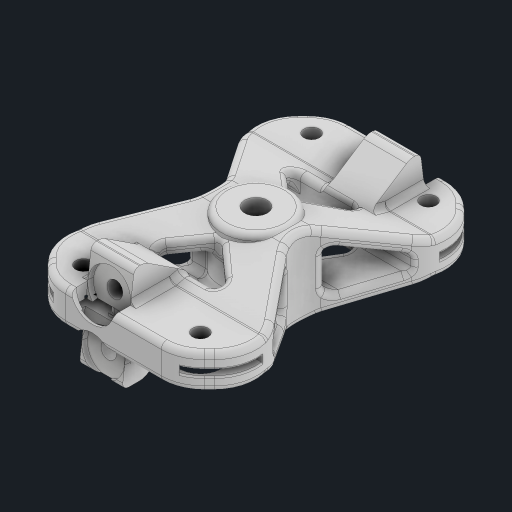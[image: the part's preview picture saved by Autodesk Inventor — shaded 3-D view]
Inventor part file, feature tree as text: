
AUTODESK INVENTOR PART (.ipt)
format: ipt  version: 2023 (Build 270158000, 158)  size: 2,082,816 bytes
history: native  units: mm
features: extrude x25, fillet x22, sketch x9, chamfer x6, mirror x2, plane x1, loft x1, other x1
ambient origin geometry x8: Origin, YZ Plane, XZ Plane, XY Plane, X Axis, Y Axis, Z Axis, Center Point
bodies: Body1 (feature_tree)
feature tree (67):
  sketch  "Sketch1"  dims[d13=261.822mm d14=7.45mm]
  plane  "Work Plane1"
  sketch  "Sketch2"  dims[d15=27.223mm d17=1.0mm]
  extrude  "Extrusion26"  Depth=7.45mm
  extrude  "Extrusion27"  Depth=1.0mm
  loft  "Loft4"
  extrude  "Extrusion30"  Depth=1.0mm
  chamfer  "Chamfer7"  Distance=15.0mm
  chamfer  "Chamfer8"  Distance=1.0mm
  extrude  "Extrusion45"  Depth=0.5mm
  extrude  "Extrusion55"  Depth=0.5mm TaperAngle=0.0deg
  extrude  "Extrusion57"  Depth=0.5mm
  sketch  "Sketch19"  dims[d26=90.0deg]
  extrude  "Extrusion67"  Depth=0.5mm
  extrude  "Extrusion68"  Depth=0.5mm TaperAngle=0.0deg
  mirror  "Mirror6"
  extrude  "Extrusion69"  Depth=0.5mm TaperAngle=0.0deg
  chamfer  "Chamfer18"  Distance=19.96mm
  chamfer  "Chamfer19"  Angle=90.0deg  [1 undecoded]
  chamfer  "Chamfer20"  Angle=90.0deg  [1 undecoded]
  chamfer  "Chamfer21"  Distance=2.0mm
  sketch  "Sketch23"  dims[d28=90.0deg d29=5.5mm d30=15.0mm]
  extrude  "Extrusion71"  Depth=2.0mm
  extrude  "Extrusion72"  Depth=0.5mm TaperAngle=45.0deg
  fillet  "Fillet54"  Radius=12.0mm
  extrude  "Extrusion73"  Depth=15.0mm
  sketch  "Sketch24"  dims[d31=65.0mm]
  extrude  "Extrusion74"  Depth=0.5mm TaperAngle=0.0deg
  extrude  "Extrusion75"  Depth=0.5mm
  extrude  "Extrusion76"  Depth=0.5mm
  fillet  "Fillet55"  Radius=10.0mm
  fillet  "Fillet56"  Radius=100.0mm
  extrude  "Extrusion77"  Depth=0.5mm
  fillet  "Fillet58"  Radius=5.0mm
  extrude  "Extrusion78"  Depth=0.5mm
  extrude  "Extrusion79"  Depth=0.5mm
  fillet  "Fillet59"  Radius=100.0mm
  fillet  "Fillet60"  Radius=35.0mm
  fillet  "Fillet61"  Radius=5.0mm
  fillet  "Fillet62"  Radius=5.0mm
  fillet  "Fillet64"  Radius=0.25mm
  fillet  "Fillet65"  Radius=15.0mm
  fillet  "Fillet66"  Radius=15.0mm
  fillet  "Fillet67"  Radius=30.0mm
  fillet  "Fillet68"  Radius=15.0mm
  fillet  "Fillet69"  Radius=30.0mm
  fillet  "Fillet70"  Radius=14.0mm
  fillet  "Fillet71"  Radius=14.0mm
  extrude  "Extrusion80"  Depth=0.5mm TaperAngle=45.0deg
  extrude  "Extrusion81"  Depth=0.5mm TaperAngle=45.0deg
  extrude  "Extrusion82"  Depth=15.0mm
  extrude  "Extrusion83"  Depth=15.0mm
  extrude  "Extrusion84"  Depth=15.0mm
  fillet  "Fillet72"  Radius=2.5mm
  mirror  "Mirror7"
  fillet  "Fillet73"  Radius=15.0mm
  fillet  "Fillet74"  Radius=15.0mm
  fillet  "Fillet75"  Radius=15.0mm
  fillet  "Fillet76"  Radius=15.0mm
  fillet  "Fillet77"  [1 undecoded]
  extrude  "Extrusion85"  Depth=15.0mm
  extrude  "Extrusion87"  Depth=0.5mm
  sketch  "Sketch12"  dims[d21=35.0mm d22=100.0mm]
  other  "Edges5"
  sketch  "Sketch18"  dims[d23=2.0mm d25=1.0mm]
  sketch  "Sketch21"  dims[d27=1.0mm]
  sketch  "Sketch25"  dims[d56=12.0mm d74=1.0mm d75=8.0mm d148=244.423mm d149=41.005864mm d150=244.423mm d151=5.5mm d152=5.5mm d153=5.5mm d154=15.0mm d155=15.0mm d156=18.0mm d157=5.5mm d158=160.0mm d159=7.0mm d160=0.0mm d161=8.0mm d162=24.0mm d163=30.0mm d164=0.0mm d165=5.0mm d166=0.0mm d167=19.96mm d170=0.0mm d171=90.0deg d172=0.0mm d173=90.0deg d178=2.0mm d179=0.0mm d180=2.0mm d206=12.0mm d207=12.0mm d208=45.0deg d209=12.0mm d210=12.0mm d211=45.0deg d256=15.0mm d257=30.0mm d258=0.0mm d271=14.0mm d272=100.0mm d273=10.0mm d274=100.0mm d313=5.5mm d316=5.0mm d317=5.0mm d318=16.0mm d319=100.0mm d320=0.0mm d324=35.0mm d325=0.0mm d333=5.0mm d341=5.0mm d369=0.25mm d370=0.0mm d379=15.0mm d380=0.0mm d381=15.0mm d382=0.0mm d386=30.0mm d392=15.0mm d394=30.0mm d395=0.0mm d396=14.0mm d397=9.1686mm d398=45.0deg d399=14.0mm d400=9.1686mm d401=45.0deg d402=10.83mm d403=14.0mm d404=45.0deg d405=10.9mm d406=14.0mm d407=45.0deg d418=15.0mm d419=15.0mm d420=15.0mm d421=2.5mm d422=15.0mm d423=15.0mm d424=15.0mm d425=15.0mm d426=90.0deg d427=15.0mm d428=5.5mm d429=15.0mm d430=5.5mm d435=18.0mm d436=0.0mm d437=15.0mm d438=0.0mm d439=2.0mm d440=15.0mm d441=2.0mm d442=0.0mm d443=0.0mm d444=15.0mm d445=15.0mm d446=15.0mm d447=2.5mm d448=15.0mm d449=15.0mm d450=15.0mm d451=90.0deg d452=15.0mm d453=90.0deg d454=15.0mm d455=5.5mm d456=15.0mm d457=5.5mm d458=15.0mm d459=2.0mm d460=0.0mm d461=0.0mm d462=18.0mm d463=0.0mm d464=15.0mm d465=0.0mm d466=10.0mm d467=15.0mm d469=20.0mm d470=1.0mm d471=30.0mm d472=0.0mm d473=2.0mm d474=20.0mm d475=0.0mm d476=35.0mm d477=0.0mm d478=20.0mm d479=2.0mm d480=2.0mm d481=2.0mm d483=2.0mm d484=2.0mm d485=2.0mm d486=2.0mm d487=2.0mm d488=2.0mm d489=2.0mm d490=2.0mm d491=10.0mm d492=0.0mm d493=10.0mm d494=0.0mm d495=3.0mm d496=0.0mm d498=90.0deg d499=10.0mm d500=0.0mm d501=2.0mm d502=0.0mm d503=2.0mm d504=5.0mm d505=2.0mm d506=2.0mm d507=2.0mm d508=0.5mm d509=1.218294mm d510=15.0mm d511=0.0mm d514=2.0mm d515=2.0mm d516=15.0mm d517=0.0mm d76=0.5mm d77=0.872665mm d144=0.5mm d145=0.872665mm d146=0.5mm d147=0.872665mm d241=0.0mm d242=0.0mm d243=0.0mm d244=0.0mm d268=0.0mm d269=0.0mm d270=0.0mm d342=0.872665mm d343=0.5mm d344=0.872665mm d348=0.0mm d349=0.0mm d350=0.0mm d351=0.0mm d352=0.0mm d353=0.0mm d354=0.0mm d357=0.0mm d358=0.0mm d359=0.0mm d360=0.0mm d512=0.5mm d513=0.872665mm]
note: 3 required parameter values undecoded (feature->parameter linkage not recoverable at this tier; creation-order binding heuristic only, values carry confidence <= 0.55)
